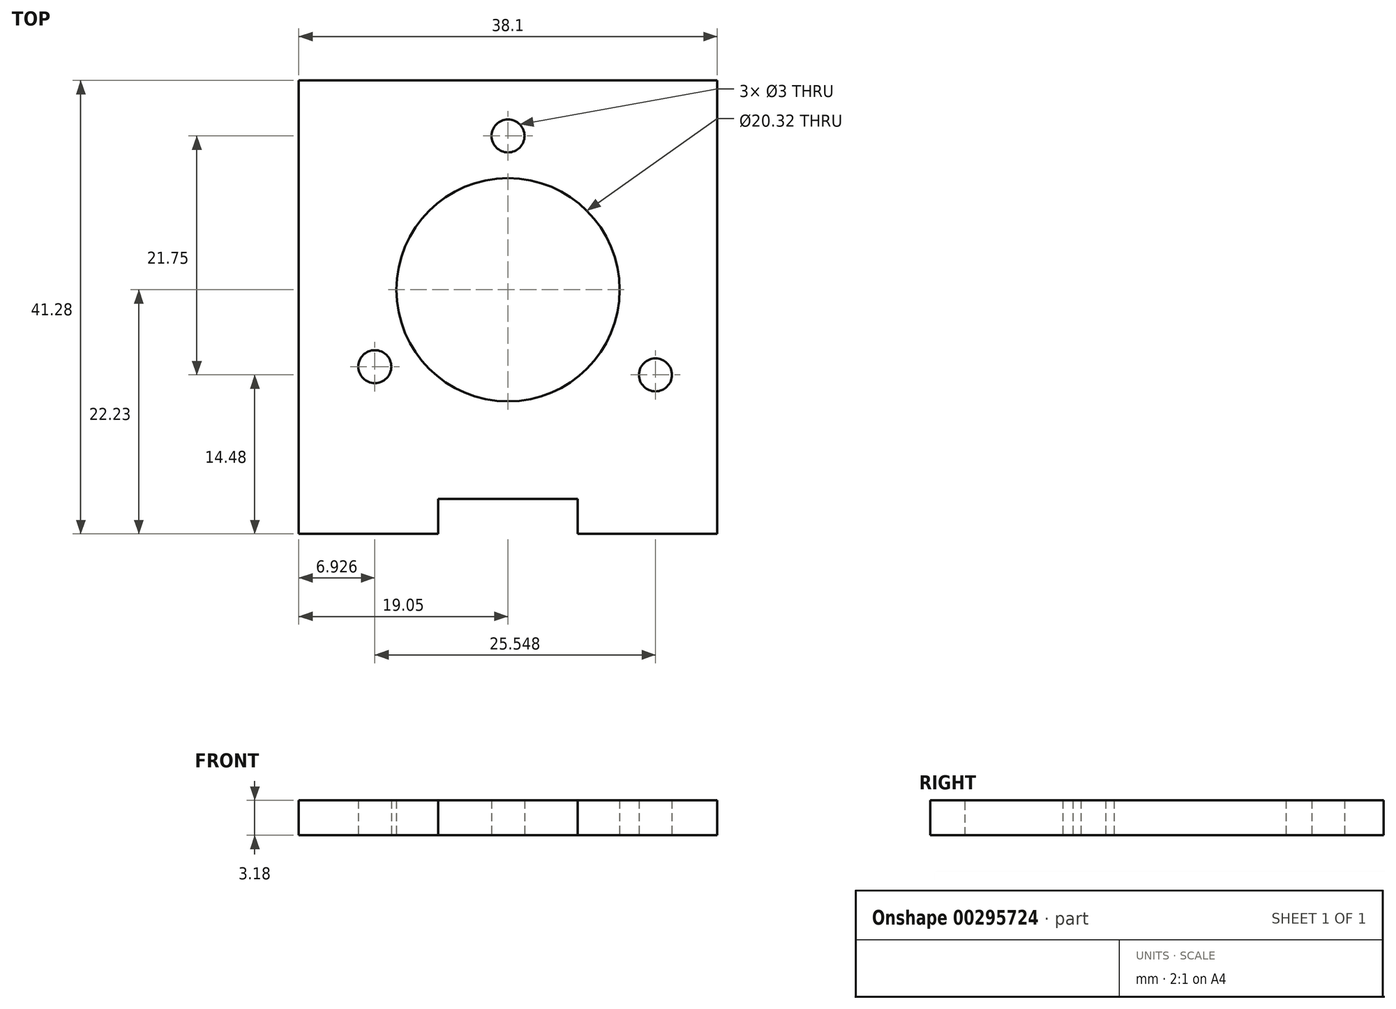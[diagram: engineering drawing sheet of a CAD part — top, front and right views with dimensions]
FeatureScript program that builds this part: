
annotation { "Feature Type Name" : "Feature", "Feature Type Description" : "" }
export const myFeature = defineFeature(function(context is Context, id is Id, definition is map)
    precondition{}
    {
        {
            var Q0;
            Q0=qCreatedBy(makeId("Top.planeOp"),FACE);
            var sketch = newSketch(context, id + "F0", { "sketchPlane" : qUnion([Q0])});
            skLineSegment(sketch, "E0.bottom", {"start": v(19.05, -19.05) * mm, "end": v(-19.05, -19.05) * mm});
            skLineSegment(sketch, "E0.top", {"start": v(19.05, 19.05) * mm, "end": v(-19.05, 19.05) * mm});
            skLineSegment(sketch, "E0.left", {"start": v(19.05, -19.05) * mm, "end": v(19.05, 19.05) * mm});
            skLineSegment(sketch, "E0.right", {"start": v(-19.05, -19.05) * mm, "end": v(-19.05, 19.05) * mm});
            skPoint(sketch, "E0.middle", {"position": v(0, 0) * mm});
            skCircle(sketch, "E1", {"center": v(0, 0) * mm, "radius": 10.16 * mm});
            skLineSegment(sketch, "E2", {"start": v(0, 0) * mm, "end": v(0, 33.18) * mm});
            skLineSegment(sketch, "E3", {"start": v(0, 0) * mm, "end": v(27.73, -16) * mm});
            skLineSegment(sketch, "E4", {"start": v(0, 0) * mm, "end": v(-24.39, -14.08) * mm});
            skCircle(sketch, "E5", {"center": v(-12.12, -7) * mm, "radius": 1.5 * mm});
            skCircle(sketch, "E6", {"center": v(0, 14) * mm, "radius": 1.5 * mm});
            skCircle(sketch, "E7", {"center": v(13.42, -7.75) * mm, "radius": 1.5 * mm});
            skSolve(sketch);
        }
        {
            var Q0;
            Q0 = qSketchRegion(id + "F0", true);
            extrude(context, id + "F1", {"entities" : qUnion([Q0]), "depth" : 3.17 * mm});
        }
        {
            var Q0;
            Q0=makeQuery(id+"F1.opExtrude","SWEPT_FACE",FACE,{"disambiguationData":[OSD([sQuery(id+"F0.wireOp",EDGE,"E0.bottom")])]});
            var sketch = newSketch(context, id + "F2", { "sketchPlane" : qUnion([Q0])});
            skLineSegment(sketch, "E8.bottom", {"start": v(-19.05, 3.18) * mm, "end": v(-6.35, 3.18) * mm});
            skLineSegment(sketch, "E8.top", {"start": v(-19.05, 0) * mm, "end": v(-6.35, 0) * mm});
            skLineSegment(sketch, "E8.left", {"start": v(-19.05, 3.18) * mm, "end": v(-19.05, 0) * mm});
            skLineSegment(sketch, "E8.right", {"start": v(-6.35, 3.18) * mm, "end": v(-6.35, 0) * mm});
            skLineSegment(sketch, "E9.bottom", {"start": v(-6.35, 0) * mm, "end": v(6.35, 0) * mm});
            skLineSegment(sketch, "E9.top", {"start": v(-6.35, 3.18) * mm, "end": v(6.35, 3.18) * mm});
            skLineSegment(sketch, "E9.left", {"start": v(-6.35, 0) * mm, "end": v(-6.35, 3.18) * mm});
            skLineSegment(sketch, "E9.right", {"start": v(6.35, 0) * mm, "end": v(6.35, 3.18) * mm});
            skLineSegment(sketch, "E10.bottom", {"start": v(6.35, 3.18) * mm, "end": v(19.05, 3.18) * mm});
            skLineSegment(sketch, "E10.top", {"start": v(6.35, 0) * mm, "end": v(19.05, 0) * mm});
            skLineSegment(sketch, "E10.left", {"start": v(6.35, 3.18) * mm, "end": v(6.35, 0) * mm});
            skLineSegment(sketch, "E10.right", {"start": v(19.05, 3.18) * mm, "end": v(19.05, 0) * mm});
            skSolve(sketch);
        }
        {
            var Q0;
            Q0=makeQuery(id+"F2.imprint","IMPRINT",FACE,{"disambiguationData":[TD([[makeQuery(id+"F2.imprint","IMPRINT",EDGE,{"derivedFrom":sQuery(id+"F2.wireOp",EDGE,"E8.bottom")}),1.0]])]});
            var Q1;
            Q1=makeQuery(id+"F2.imprint","IMPRINT",FACE,{"disambiguationData":[TD([[makeQuery(id+"F2.imprint","IMPRINT",EDGE,{"derivedFrom":sQuery(id+"F2.wireOp",EDGE,"E10.bottom")}),1.0]])]});
            extrude(context, id + "F3", {"entities" : qUnion([Q0, Q1]), "operationType" : NewBodyOperationType.ADD, "depth" : 3.17 * mm});
        }
    });
